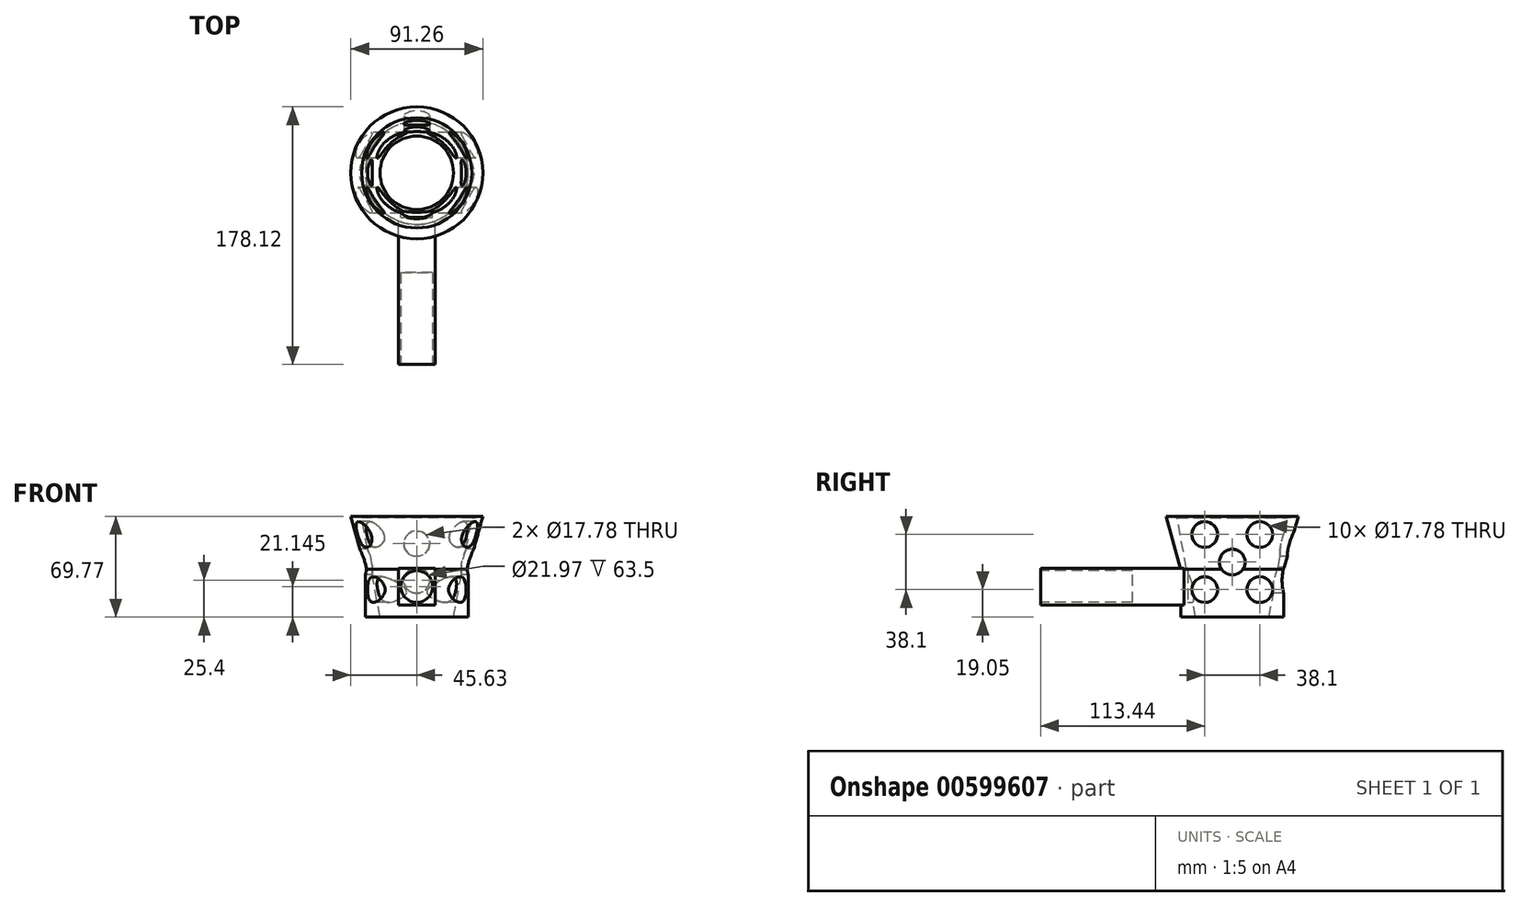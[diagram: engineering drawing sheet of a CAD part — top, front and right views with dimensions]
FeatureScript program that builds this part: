
annotation { "Feature Type Name" : "Feature", "Feature Type Description" : "" }
export const myFeature = defineFeature(function(context is Context, id is Id, definition is map)
    precondition{}
    {
        {
            var Q0;
            Q0=qCreatedBy(makeId("Front.planeOp"),FACE);
            var sketch = newSketch(context, id + "F0", { "sketchPlane" : qUnion([Q0])});
            skLineSegment(sketch, "E0", {"start": v(-38.1, 68.58) * mm, "end": v(-25.4, 0) * mm});
            skLineSegment(sketch, "E1", {"start": v(0, 102.34) * mm, "end": v(0, -100.86) * mm, "construction": true});
            skLineSegment(sketch, "E2", {"start": v(-38.1, 68.58) * mm, "end": v(-25.4, 68.58) * mm, "construction": true});
            skLineSegment(sketch, "E3", {"start": v(-25.4, 68.58) * mm, "end": v(-25.4, 0) * mm, "construction": true});
            skLineSegment(sketch, "E4", {"start": v(-25.4, 0) * mm, "end": v(-35.56, 0) * mm});
            skLineSegment(sketch, "E5", {"start": v(-35.56, 0) * mm, "end": v(-35.56, 33.02) * mm});
            skLineSegment(sketch, "E6", {"start": v(-35.56, 33.02) * mm, "end": v(-45.63, 69.77) * mm});
            skLineSegment(sketch, "E7", {"start": v(-38.1, 68.58) * mm, "end": v(-45.63, 69.77) * mm});
            skSolve(sketch);
        }
        {
            var Q0;
            Q0=qSketchRegion(id+"F0",true);
            var Q1;
            Q1=sQuery(id+"F0.wireOp",EDGE,"E1");
            revolve(context, id + "F1", {"entities" : qUnion([Q0]), "axis" : qUnion([Q1]), "revolveType" : RevolveType.FULL});
        }
        {
            var Q0;
            Q0=qCreatedBy(makeId("Front.planeOp"),FACE);
            var sketch = newSketch(context, id + "F2", { "sketchPlane" : qUnion([Q0])});
            skCircle(sketch, "E8", {"center": v(0, 21.15) * mm, "radius": 10.99 * mm});
            skSolve(sketch);
        }
        {
            var Q0;
            Q0=qSketchRegion(id+"F2",true);
            extrude(context, id + "F3", {"entities" : qUnion([Q0]), "operationType" : NewBodyOperationType.REMOVE, "depth" : 35.05 * mm, "offsetDistance" : 25.4 * mm});
        }
        {
            var Q0;
            Q0=makeQuery(id+"F3.boolean.opBoolean","COPY",FACE,{"derivedFrom":makeQuery(id+"F3.opExtrude","CAP_FACE",FACE,{"disambiguationData":[OSD([sQuery(id+"F2.wireOp",EDGE,"E8")])],"isStart":false})});
            var sketch = newSketch(context, id + "F4", { "sketchPlane" : qUnion([Q0])});
            skCircle(sketch, "E9", {"center": v(0, 21.15) * mm, "radius": 12.7 * mm});
            skSolve(sketch);
        }
        {
            var Q0;
            Q0=qSketchRegion(id+"F4",true);
            extrude(context, id + "F5", {"entities" : qUnion([Q0]), "operationType" : NewBodyOperationType.ADD, "depth" : 4.17 * mm, "offsetDistance" : 25.4 * mm, "hasSecondDirection" : true, "secondDirectionOppositeDirection" : true, "secondDirectionDepth" : 2.03 * mm});
        }
        {
            var Q0;
            Q0=makeQuery(id+"F5.opExtrude","CAP_FACE",FACE,{"disambiguationData":[OSD([sQuery(id+"F4.wireOp",EDGE,"E9")])],"isStart":false});
            var sketch = newSketch(context, id + "F6", { "sketchPlane" : qUnion([Q0])});
            skPoint(sketch, "E10", {"position": v(0, 21.15) * mm});
            skCircle(sketch, "E11", {"center": v(0, 21.15) * mm, "radius": 12.7 * mm, "construction": true});
            skLineSegment(sketch, "E12", {"start": v(0, 33.85) * mm, "end": v(0, 8.45) * mm, "construction": true});
            skLineSegment(sketch, "E13", {"start": v(12.7, 21.15) * mm, "end": v(-12.7, 21.15) * mm, "construction": true});
            skLineSegment(sketch, "E14.bottom", {"start": v(-12.7, 33.85) * mm, "end": v(12.7, 33.85) * mm});
            skLineSegment(sketch, "E14.top", {"start": v(-12.7, 8.45) * mm, "end": v(12.7, 8.45) * mm});
            skLineSegment(sketch, "E14.left", {"start": v(-12.7, 33.85) * mm, "end": v(-12.7, 8.45) * mm});
            skLineSegment(sketch, "E14.right", {"start": v(12.7, 33.85) * mm, "end": v(12.7, 8.45) * mm});
            skSolve(sketch);
        }
        {
            var Q0;
            Q0=qSketchRegion(id+"F6",true);
            extrude(context, id + "F7", {"entities" : qUnion([Q0]), "operationType" : NewBodyOperationType.ADD, "oppositeDirection" : true, "depth" : 101.6 * mm, "offsetDistance" : 25.4 * mm});
        }
        {
            var Q0;
            Q0=qCreatedBy(makeId("Right.planeOp"),FACE);
            var sketch = newSketch(context, id + "F8", { "sketchPlane" : qUnion([Q0])});
            skCircle(sketch, "E15", {"center": v(19.05, 57.15) * mm, "radius": 8.9 * mm});
            skCircle(sketch, "E16", {"center": v(-19.05, 57.15) * mm, "radius": 8.9 * mm});
            skCircle(sketch, "E17", {"center": v(19.05, 19.05) * mm, "radius": 8.9 * mm});
            skCircle(sketch, "E18", {"center": v(-19.05, 19.05) * mm, "radius": 8.9 * mm});
            skCircle(sketch, "E19", {"center": v(0, 38.1) * mm, "radius": 8.9 * mm});
            skLineSegment(sketch, "E20", {"start": v(19.05, 57.15) * mm, "end": v(-19.05, 57.15) * mm, "construction": true});
            skLineSegment(sketch, "E21", {"start": v(-19.05, 57.15) * mm, "end": v(-19.05, 19.05) * mm, "construction": true});
            skLineSegment(sketch, "E22", {"start": v(-19.05, 19.05) * mm, "end": v(19.05, 19.05) * mm, "construction": true});
            skLineSegment(sketch, "E23", {"start": v(19.05, 19.05) * mm, "end": v(19.05, 57.15) * mm, "construction": true});
            skLineSegment(sketch, "E24", {"start": v(0, 38.1) * mm, "end": v(19.05, 57.15) * mm});
            skLineSegment(sketch, "E25", {"start": v(-19.05, 57.15) * mm, "end": v(0, 38.1) * mm});
            skLineSegment(sketch, "E26", {"start": v(-19.05, 19.05) * mm, "end": v(0, 38.1) * mm});
            skLineSegment(sketch, "E27", {"start": v(19.05, 19.05) * mm, "end": v(0, 38.1) * mm});
            skSolve(sketch);
        }
        {
            var Q0;
            Q0=qSketchRegion(id+"F8",true);
            extrude(context, id + "F9", {"entities" : qUnion([Q0]), "operationType" : NewBodyOperationType.REMOVE, "endBound" : BoundingType.SYMMETRIC, "depth" : 105.16 * mm, "offsetDistance" : 25.4 * mm});
        }
        {
            var Q0;
            Q0=qCreatedBy(makeId("Front.planeOp"),FACE);
            var sketch = newSketch(context, id + "F10", { "sketchPlane" : qUnion([Q0])});
            skCircle(sketch, "E28", {"center": v(0, 50.8) * mm, "radius": 8.9 * mm});
            skCircle(sketch, "E29", {"center": v(0, 25.4) * mm, "radius": 8.9 * mm});
            skLineSegment(sketch, "E30", {"start": v(0, 25.4) * mm, "end": v(0, 50.8) * mm, "construction": true});
            skLineSegment(sketch, "E31", {"start": v(0, 25.4) * mm, "end": v(0, 0) * mm, "construction": true});
            skSolve(sketch);
        }
        {
            var Q0;
            Q0=qSketchRegion(id+"F10",true);
            extrude(context, id + "F11", {"entities" : qUnion([Q0]), "operationType" : NewBodyOperationType.REMOVE, "oppositeDirection" : true, "depth" : 79.76 * mm, "offsetDistance" : 25.4 * mm});
        }
        {
            var Q0;
            Q0=makeQuery(id+"F7.opExtrude","CAP_FACE",FACE,{"disambiguationData":[OSD([sQuery(id+"F6.wireOp",EDGE,"E14.bottom"),sQuery(id+"F6.wireOp",EDGE,"E14.top"),sQuery(id+"F6.wireOp",EDGE,"E14.left"),sQuery(id+"F6.wireOp",EDGE,"E14.right")])],"isStart":false});
            var sketch = newSketch(context, id + "F12", { "sketchPlane" : qUnion([Q0])});
            skLineSegment(sketch, "E32", {"start": v(-12.7, 33.85) * mm, "end": v(12.7, 8.45) * mm, "construction": true});
            skLineSegment(sketch, "E33", {"start": v(12.7, 33.85) * mm, "end": v(-12.7, 8.45) * mm, "construction": true});
            skCircle(sketch, "E34", {"center": v(0, 21.15) * mm, "radius": 10.99 * mm});
            skSolve(sketch);
        }
        {
            var Q0;
            Q0 = qSketchRegion(id + "F12", true);
            extrude(context, id + "F13", {"entities" : qUnion([Q0]), "operationType" : NewBodyOperationType.REMOVE, "oppositeDirection" : true, "depth" : 63.5 * mm, "offsetDistance" : 25.4 * mm});
        }
    });
